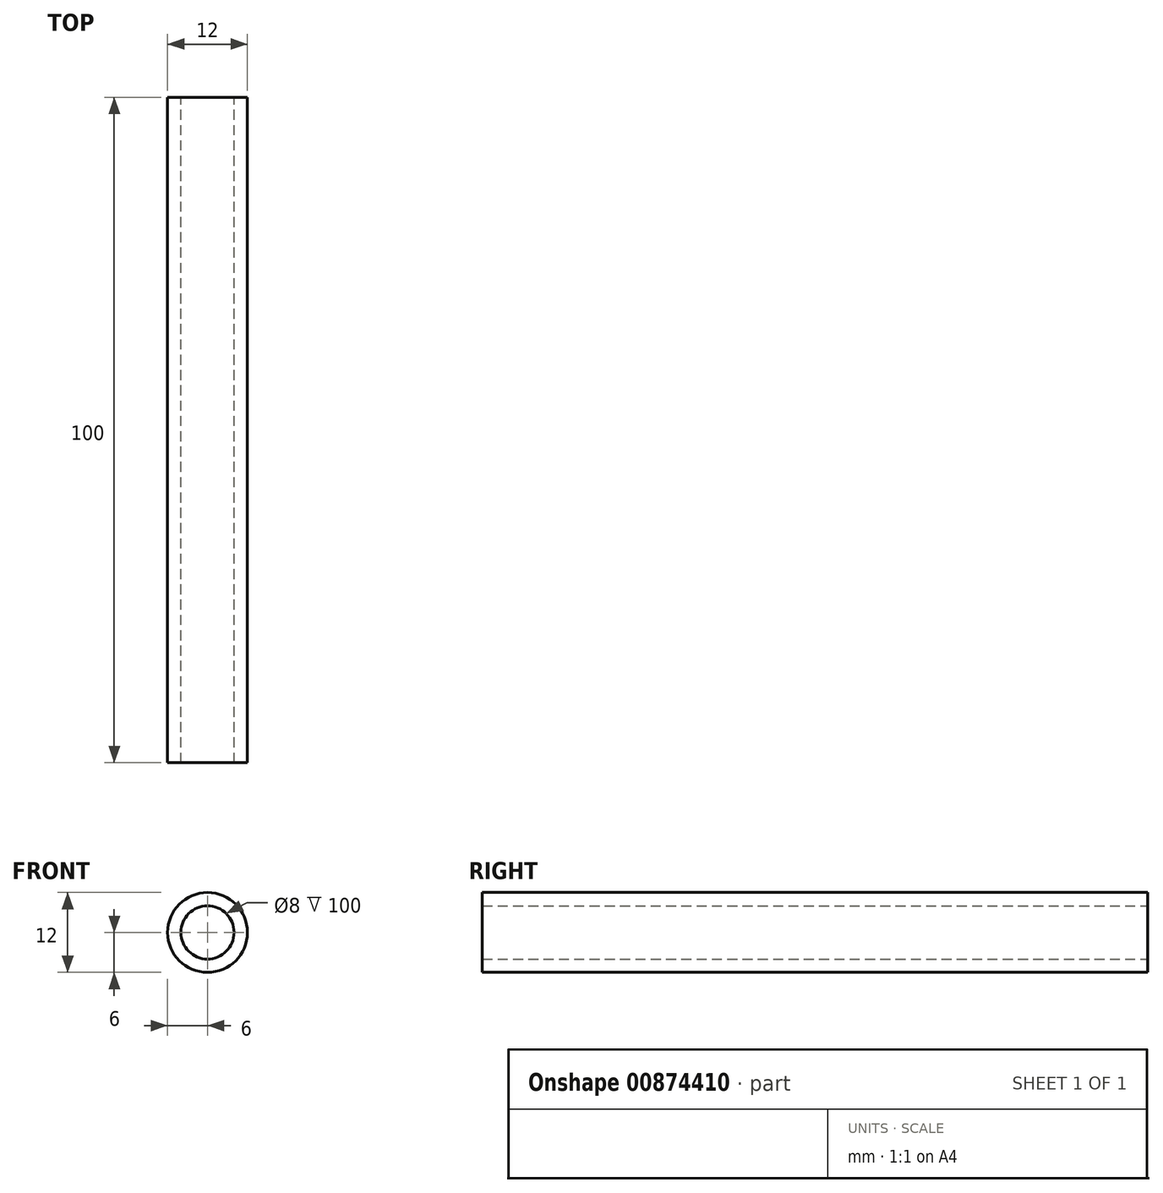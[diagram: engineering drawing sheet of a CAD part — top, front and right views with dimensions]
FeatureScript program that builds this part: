
annotation { "Feature Type Name" : "Feature", "Feature Type Description" : "" }
export const myFeature = defineFeature(function(context is Context, id is Id, definition is map)
    precondition{}
    {
        {
            var Q0;
            Q0=qCreatedBy(makeId("Front.planeOp"),FACE);
            var sketch = newSketch(context, id + "F0", { "sketchPlane" : qUnion([Q0])});
            skCircle(sketch, "E0", {"center": v(0, 0) * mm, "radius": 6 * mm});
            skCircle(sketch, "E1", {"center": v(0, 0) * mm, "radius": 4 * mm});
            skSolve(sketch);
        }
        {
            var Q0;
            Q0 = qSketchRegion(id + "F0", true);
            extrude(context, id + "F1", {"entities" : qUnion([Q0]), "depth" : 100 * mm, "offsetDistance" : 25 * mm});
        }
    });
